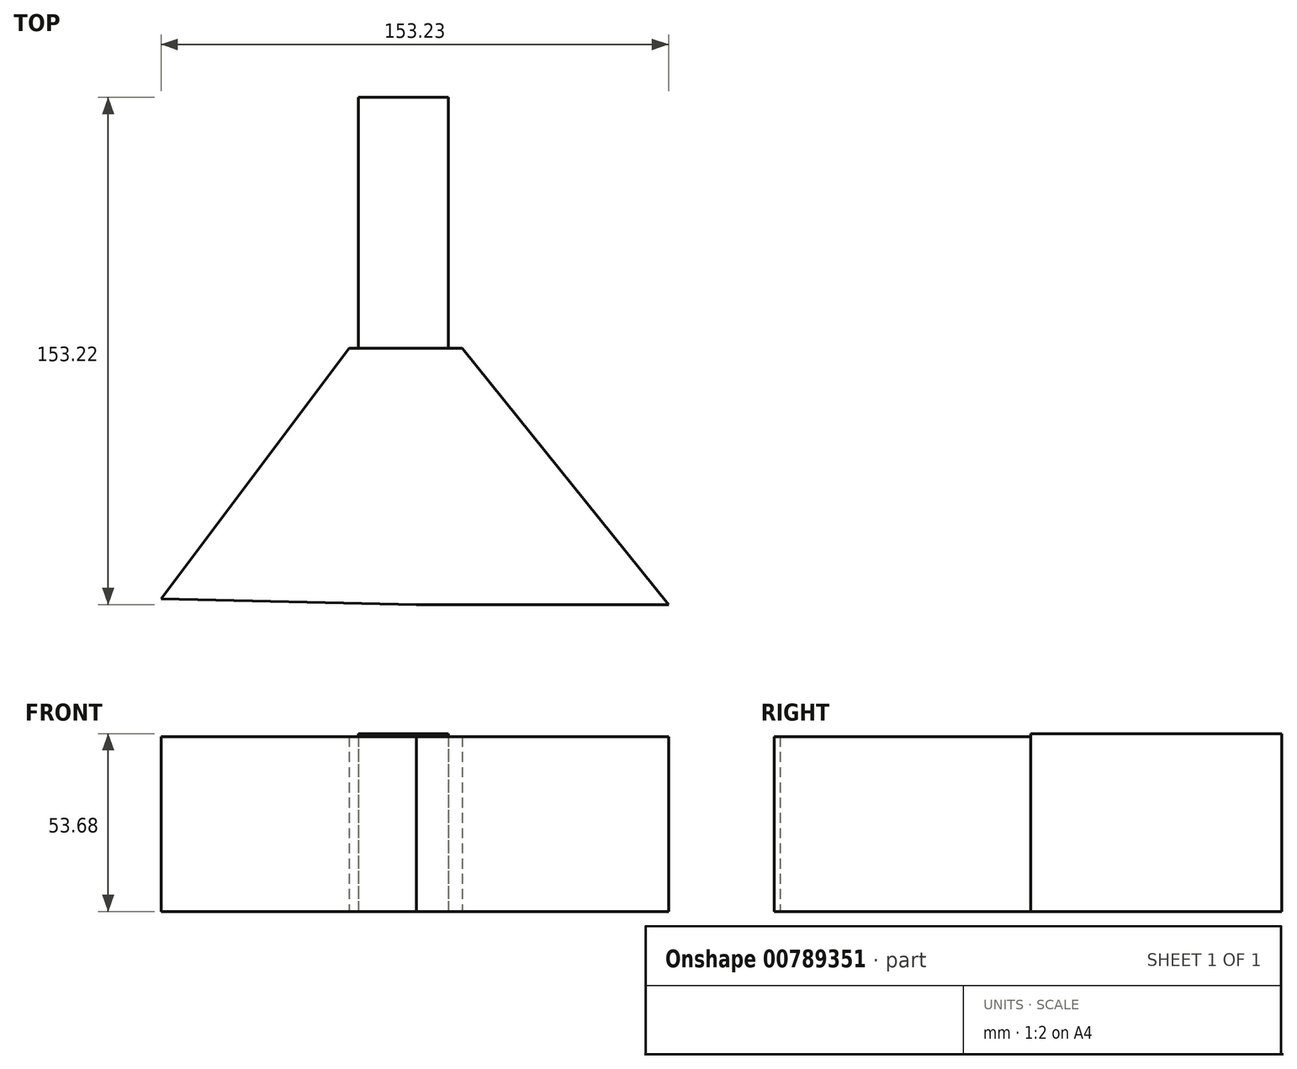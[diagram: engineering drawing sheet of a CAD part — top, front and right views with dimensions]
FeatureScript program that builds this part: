
annotation { "Feature Type Name" : "Feature", "Feature Type Description" : "" }
export const myFeature = defineFeature(function(context is Context, id is Id, definition is map)
    precondition{}
    {
        {
            var Q0;
            Q0=qCreatedBy(makeId("Top.planeOp"),FACE);
            var sketch = newSketch(context, id + "F0", { "sketchPlane" : qUnion([Q0])});
            skLineSegment(sketch, "E0", {"start": v(13.83, 0) * mm, "end": v(0, 0) * mm});
            skLineSegment(sketch, "E1", {"start": v(0, 0) * mm, "end": v(0, -77.4) * mm});
            skLineSegment(sketch, "E2", {"start": v(0, -77.4) * mm, "end": v(76.17, -77.4) * mm});
            skLineSegment(sketch, "E3", {"start": v(76.17, -77.4) * mm, "end": v(13.83, 0) * mm});
            skLineSegment(sketch, "E4", {"start": v(-20.29, 0) * mm, "end": v(0, 0) * mm});
            skLineSegment(sketch, "E5", {"start": v(-20.29, 0) * mm, "end": v(-77.06, -75.7) * mm});
            skLineSegment(sketch, "E6", {"start": v(-77.06, -75.7) * mm, "end": v(0, -77.4) * mm});
            skSolve(sketch);
        }
        {
            var Q0;
            Q0=makeQuery(id+"F0.imprint","IMPRINT",FACE,{"disambiguationData":[TD([[makeQuery(id+"F0.imprint","IMPRINT",EDGE,{"derivedFrom":sQuery(id+"F0.wireOp",EDGE,"E0")}),1.0]])]});
            var Q1;
            Q1 = qSketchRegion(id + "F0", true);
            extrude(context, id + "F1", {"entities" : qUnion([Q0, Q1]), "depth" : 27.35 * mm, "offsetDistance" : 25.4 * mm});
        }
        {
            var Q0;
            Q0=makeQuery(id+"F1.opExtrude","CAP_FACE",FACE,{"disambiguationData":[OSD([sQuery(id+"F0.wireOp",EDGE,"E0"),sQuery(id+"F0.wireOp",EDGE,"E2"),sQuery(id+"F0.wireOp",EDGE,"E3"),sQuery(id+"F0.wireOp",EDGE,"E4"),sQuery(id+"F0.wireOp",EDGE,"E5"),sQuery(id+"F0.wireOp",EDGE,"E6")])],"isStart":false});
            var Q1;
            Q1 = qSketchRegion(id + "F0", true);
            extrude(context, id + "F2", {"entities" : qUnion([Q0, Q1]), "operationType" : NewBodyOperationType.ADD, "depth" : 25.4 * mm, "offsetDistance" : 25.4 * mm});
        }
        {
            var Q0;
            Q0=qCreatedBy(makeId("Top.planeOp"),FACE);
            var sketch = newSketch(context, id + "F3", { "sketchPlane" : qUnion([Q0])});
            skLineSegment(sketch, "E7", {"start": v(-17.5, 0) * mm, "end": v(-17.5, 75.82) * mm});
            skLineSegment(sketch, "E8", {"start": v(-17.5, 75.82) * mm, "end": v(9.73, 75.82) * mm});
            skLineSegment(sketch, "E9", {"start": v(9.73, 75.82) * mm, "end": v(9.73, 0) * mm});
            skLineSegment(sketch, "E10", {"start": v(9.73, 0) * mm, "end": v(9.73, 75.82) * mm});
            skLineSegment(sketch, "E11", {"start": v(9.73, 0) * mm, "end": v(-17.5, 0) * mm});
            skSolve(sketch);
        }
        {
            var Q0;
            Q0=makeQuery(id+"F3.imprint","IMPRINT",FACE,{"disambiguationData":[TD([[makeQuery(id+"F3.imprint","IMPRINT",EDGE,{"derivedFrom":sQuery(id+"F3.wireOp",EDGE,"E7")}),-1.0]])]});
            var Q1;
            Q1 = qSketchRegion(id + "F3", true);
            extrude(context, id + "F4", {"entities" : qUnion([Q0, Q1]), "operationType" : NewBodyOperationType.ADD, "depth" : 53.68 * mm, "offsetDistance" : 25.4 * mm});
        }
    });
